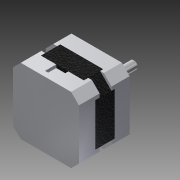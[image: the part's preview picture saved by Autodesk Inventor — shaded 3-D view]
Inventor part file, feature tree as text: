
AUTODESK INVENTOR PART (.ipt)
format: ipt  version: 2015 (Build 190159000, 159)  size: 273,920 bytes
history: native  units: mm
features: extrude x11, sketch x11, other x7, projected_geometry x5, chamfer x1
ambient origin geometry x8: Origin, YZ Plane, XZ Plane, XY Plane, X Axis, Y Axis, Z Axis, Center Point
bodies: Body1 (feature_tree), Body2 (feature_tree), Body3 (feature_tree), Body4 (feature_tree)
feature tree (35):
  other  "Bottom"
  other  "Blocks"
  extrude  "Extrusion1"  Depth=42.3mm
  extrude  "Extrusion2"  Depth=5.0mm
  extrude  "Extrusion3"  Depth=5.0mm
  extrude  "Extrusion4"  Depth=5.0mm
  extrude  "Extrusion5"  Depth=5.0mm
  extrude  "Extrusion6"  Depth=10.5mm
  extrude  "Extrusion7"  Depth=40.0mm TaperAngle=360.0deg
  extrude  "Extrusion8"  Depth=12.4mm TaperAngle=0.0deg
  extrude  "Extrusion9"  Depth=2.0mm TaperAngle=0.0deg
  extrude  "Extrusion10"  Depth=7.8mm
  chamfer  "Chamfer1"  Distance=2.0mm
  extrude  "Extrusion11"  Depth=2.0mm
  other  "captive_nut_mortises"
  other  "captive_nut_tenons"
  sketch  "Sketch3"  dims[d13=42.3mm d14=42.3mm]
  sketch  "Sketch5"  dims[d15=5.0mm d16=5.0mm]
  sketch  "Sketch6"  dims[d17=5.0mm d18=5.0mm]
  projected_geometry  "Projected Loop2"
  other  "Center"
  sketch  "Sketch7"  dims[d19=5.0mm d20=5.0mm]
  other  "Top"
  sketch  "Sketch8"  dims[d21=5.0mm d22=5.0mm]
  projected_geometry  "Projected Loop3"
  projected_geometry  "Projected Loop4"
  projected_geometry  "Projected Loop5"
  projected_geometry  "Projected Loop6"
  sketch  "Sketch9"  dims[d23=10.5mm d24=0.0mm d29=2.45mm]
  sketch  "Sketch10"  dims[d30=2.45mm d31=40.0mm d33=360.0deg]
  sketch  "Sketch11"  dims[d35=2.8mm d36=0.0mm d37=12.4mm d38=0.0mm]
  sketch  "Sketch12"  dims[d39=9.6mm d40=0.0mm d41=2.0mm d42=0.0mm]
  sketch  "Sketch13"  dims[d43=7.8mm d44=3.9mm]
  other  "Shaft"
  sketch  "Sketch14"  dims[d45=7.2mm d46=2.0mm d47=0.0mm d48=2.0mm d49=15.5mm d50=15.5mm d51=40.0mm d53=360.0deg d55=4.0mm d56=0.0mm d57=22.0mm d58=2.0mm d59=0.0mm d60=3.0mm d61=0.0mm d62=5.0mm d63=25.0mm d64=0.0mm d65=0.25mm d66=2.0mm d67=45.0deg d68=2.0mm d69=2.0mm d70=0.0mm]
